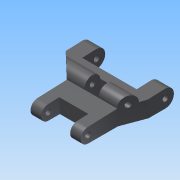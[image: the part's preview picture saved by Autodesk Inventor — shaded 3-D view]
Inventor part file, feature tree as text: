
AUTODESK INVENTOR PART (.ipt)
format: ipt  version: 2014 (Build 180170000, 170)  size: 178,688 bytes
history: native  units: in
note: dims shown in document units (in); Inventor stores cm internally (conversion verified against a paired STEP export)
features: plane x3, extrude x2, sketch x2, projected_geometry x2
ambient origin geometry x8: Origin, YZ Plane, XZ Plane, XY Plane, X Axis, Y Axis, Z Axis, Center Point
bodies: Solid1 (feature_tree)
feature tree (9):
  extrude  "Extrusion1"  Depth=1.8in TaperAngle=0.0deg
  plane  "Work Plane1"
  extrude  "Extrusion2"  Depth=0.18in
  plane  "Work Plane2"
  plane  "Work Plane3"
  sketch  "Sketch3"  dims[d5=0.115in d8=1.8in d9=0.0in]
  sketch  "Sketch5"  dims[d21=1.28in d22=0.18in d23=1.784in d24=0.0in d26=1.3in d27=0.23in d28=0.23in d29=0.4in d31=0.49in d32=0.31in d33=0.31in d34=0.4in d36=1.18in d37=0.63in d38=0.12in d39=0.157in d40=0.1875in d41=1.375in d42=0.53in d43=0.34in d44=0.354in d45=0.3005in]
  projected_geometry  "Projected Loop1"
  projected_geometry  "Project Cut Edges3"
